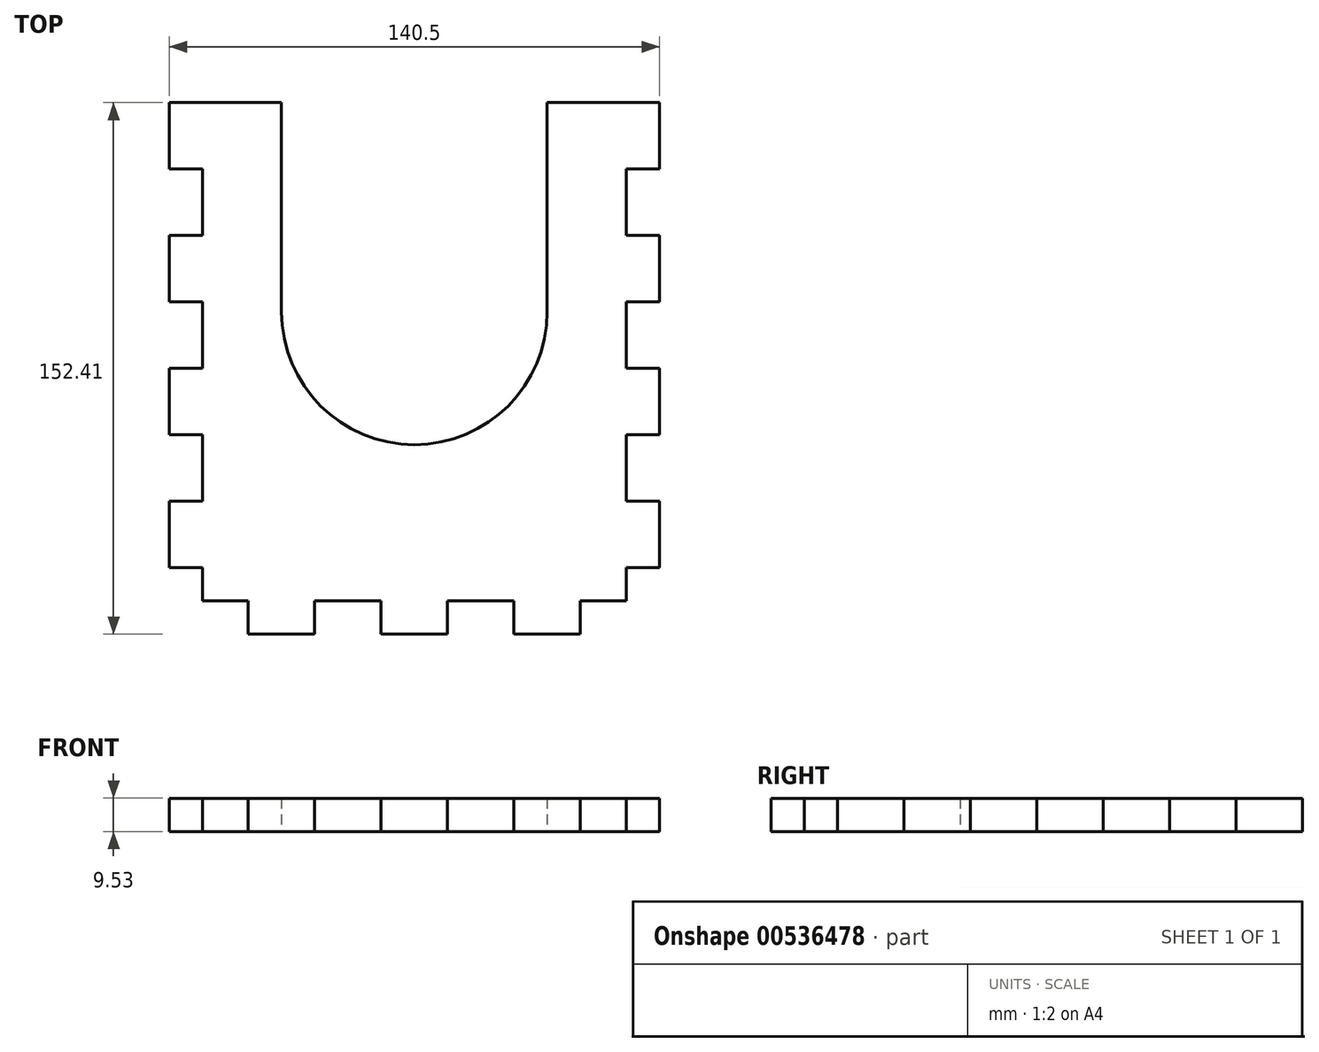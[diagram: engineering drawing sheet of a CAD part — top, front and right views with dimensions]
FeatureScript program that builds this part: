
annotation { "Feature Type Name" : "Feature", "Feature Type Description" : "" }
export const myFeature = defineFeature(function(context is Context, id is Id, definition is map)
    precondition{}
    {
        {
            var Q0;
            Q0=qCreatedBy(makeId("Top.planeOp"),FACE);
            var sketch = newSketch(context, id + "F0", { "sketchPlane" : qUnion([Q0])});
            skLineSegment(sketch, "E0", {"start": v(0, 0) * mm, "end": v(0, 9.53) * mm});
            skLineSegment(sketch, "E1", {"start": v(0, 9.53) * mm, "end": v(-9.52, 9.53) * mm});
            skLineSegment(sketch, "E2", {"start": v(-9.52, 9.52) * mm, "end": v(-9.52, 28.57) * mm});
            skLineSegment(sketch, "E3", {"start": v(-9.52, 28.57) * mm, "end": v(0, 28.57) * mm});
            skLineSegment(sketch, "E4", {"start": v(0, 28.57) * mm, "end": v(0, 47.62) * mm});
            skLineSegment(sketch, "E5", {"start": v(0, 47.62) * mm, "end": v(-9.52, 47.62) * mm});
            skLineSegment(sketch, "E6", {"start": v(-9.52, 47.62) * mm, "end": v(-9.52, 66.67) * mm});
            skLineSegment(sketch, "E7", {"start": v(-9.52, 66.67) * mm, "end": v(0, 66.67) * mm});
            skLineSegment(sketch, "E8", {"start": v(0, 66.67) * mm, "end": v(0, 85.72) * mm});
            skLineSegment(sketch, "E9", {"start": v(0, 85.72) * mm, "end": v(-9.52, 85.72) * mm});
            skLineSegment(sketch, "E10", {"start": v(-9.52, 85.72) * mm, "end": v(-9.52, 104.77) * mm});
            skLineSegment(sketch, "E11", {"start": v(-9.52, 104.77) * mm, "end": v(0, 104.77) * mm});
            skLineSegment(sketch, "E12", {"start": v(0, 104.77) * mm, "end": v(0, 123.82) * mm});
            skLineSegment(sketch, "E13", {"start": v(0, 123.82) * mm, "end": v(-9.52, 123.82) * mm});
            skLineSegment(sketch, "E14", {"start": v(-9.52, 123.82) * mm, "end": v(-9.52, 142.87) * mm});
            skLineSegment(sketch, "E15", {"start": v(22.62, 142.87) * mm, "end": v(22.62, 82.9) * mm});
            skArc(sketch, "E16", {"start": v(22.62, 82.9) * mm, "mid": v(60.72, 44.8) * mm, "end": v(98.82, 82.9) * mm});
            skLineSegment(sketch, "E17", {"start": v(98.82, 82.9) * mm, "end": v(98.82, 142.87) * mm});
            skLineSegment(sketch, "E18", {"start": v(130.97, 142.88) * mm, "end": v(130.97, 123.83) * mm});
            skLineSegment(sketch, "E19", {"start": v(130.97, 123.82) * mm, "end": v(121.44, 123.82) * mm});
            skLineSegment(sketch, "E20", {"start": v(121.44, 123.83) * mm, "end": v(121.44, 104.78) * mm});
            skLineSegment(sketch, "E21", {"start": v(121.44, 104.77) * mm, "end": v(130.97, 104.77) * mm});
            skLineSegment(sketch, "E22", {"start": v(130.97, 104.78) * mm, "end": v(130.97, 85.73) * mm});
            skLineSegment(sketch, "E23", {"start": v(130.97, 85.72) * mm, "end": v(121.44, 85.72) * mm});
            skLineSegment(sketch, "E24", {"start": v(121.44, 85.73) * mm, "end": v(121.44, 66.68) * mm});
            skLineSegment(sketch, "E25", {"start": v(121.44, 66.67) * mm, "end": v(130.97, 66.67) * mm});
            skLineSegment(sketch, "E26", {"start": v(130.97, 66.68) * mm, "end": v(130.97, 47.63) * mm});
            skLineSegment(sketch, "E27", {"start": v(130.97, 47.63) * mm, "end": v(121.44, 47.63) * mm});
            skLineSegment(sketch, "E28", {"start": v(121.44, 47.63) * mm, "end": v(121.44, 28.58) * mm});
            skLineSegment(sketch, "E29", {"start": v(121.44, 28.57) * mm, "end": v(130.97, 28.57) * mm});
            skLineSegment(sketch, "E30", {"start": v(130.97, 28.58) * mm, "end": v(130.97, 9.53) * mm});
            skLineSegment(sketch, "E31", {"start": v(130.97, 9.53) * mm, "end": v(121.44, 9.53) * mm});
            skLineSegment(sketch, "E32", {"start": v(121.44, 9.53) * mm, "end": v(121.44, 0) * mm});
            skLineSegment(sketch, "E33", {"start": v(121.44, 0) * mm, "end": v(108.35, 0) * mm});
            skLineSegment(sketch, "E34", {"start": v(108.35, 0) * mm, "end": v(108.35, -9.53) * mm});
            skLineSegment(sketch, "E35", {"start": v(108.35, -9.53) * mm, "end": v(89.3, -9.53) * mm});
            skLineSegment(sketch, "E36", {"start": v(89.3, -9.53) * mm, "end": v(89.3, 0) * mm});
            skLineSegment(sketch, "E37", {"start": v(89.3, 0) * mm, "end": v(70.25, 0) * mm});
            skLineSegment(sketch, "E38", {"start": v(70.25, 0) * mm, "end": v(70.25, -9.53) * mm});
            skLineSegment(sketch, "E39", {"start": v(70.25, -9.53) * mm, "end": v(51.2, -9.53) * mm});
            skLineSegment(sketch, "E40", {"start": v(51.2, -9.53) * mm, "end": v(51.2, 0) * mm});
            skLineSegment(sketch, "E41", {"start": v(51.2, 0) * mm, "end": v(32.15, 0) * mm});
            skLineSegment(sketch, "E42", {"start": v(32.15, 0) * mm, "end": v(32.15, -9.53) * mm});
            skLineSegment(sketch, "E43", {"start": v(32.15, -9.53) * mm, "end": v(13.1, -9.53) * mm});
            skLineSegment(sketch, "E44", {"start": v(13.1, -9.53) * mm, "end": v(13.1, 0) * mm});
            skLineSegment(sketch, "E45", {"start": v(13.1, 0) * mm, "end": v(0, 0) * mm});
            skLineSegment(sketch, "E46", {"start": v(60.72, -9.53) * mm, "end": v(60.72, 82.9) * mm, "construction": true});
            skLineSegment(sketch, "E47.top", {"start": v(-9.52, 142.87) * mm, "end": v(22.62, 142.87) * mm});
            skLineSegment(sketch, "E47.left", {"start": v(-9.52, 142.87) * mm, "end": v(-9.52, 142.87) * mm});
            skLineSegment(sketch, "E47.right", {"start": v(22.62, 142.87) * mm, "end": v(22.62, 142.87) * mm});
            skLineSegment(sketch, "E48.top", {"start": v(98.82, 142.87) * mm, "end": v(130.97, 142.87) * mm});
            skLineSegment(sketch, "E48.left", {"start": v(98.82, 142.87) * mm, "end": v(98.82, 142.88) * mm});
            skLineSegment(sketch, "E48.right", {"start": v(130.97, 142.88) * mm, "end": v(130.97, 142.88) * mm});
            skLineSegment(sketch, "E49", {"start": v(-9.53, 142.87) * mm, "end": v(22.62, 142.87) * mm, "construction": true});
            skSolve(sketch);
        }
        {
            var Q0;
            Q0=makeQuery(id+"F0.imprint","IMPRINT",FACE,{"disambiguationData":[TD([[makeQuery(id+"F0.imprint","IMPRINT",EDGE,{"derivedFrom":sQuery(id+"F0.wireOp",EDGE,"E0")}),-1.0]])]});
            extrude(context, id + "F1", {"entities" : qUnion([Q0]), "depth" : 9.52 * mm, "offsetDistance" : 25.4 * mm});
        }
    });
